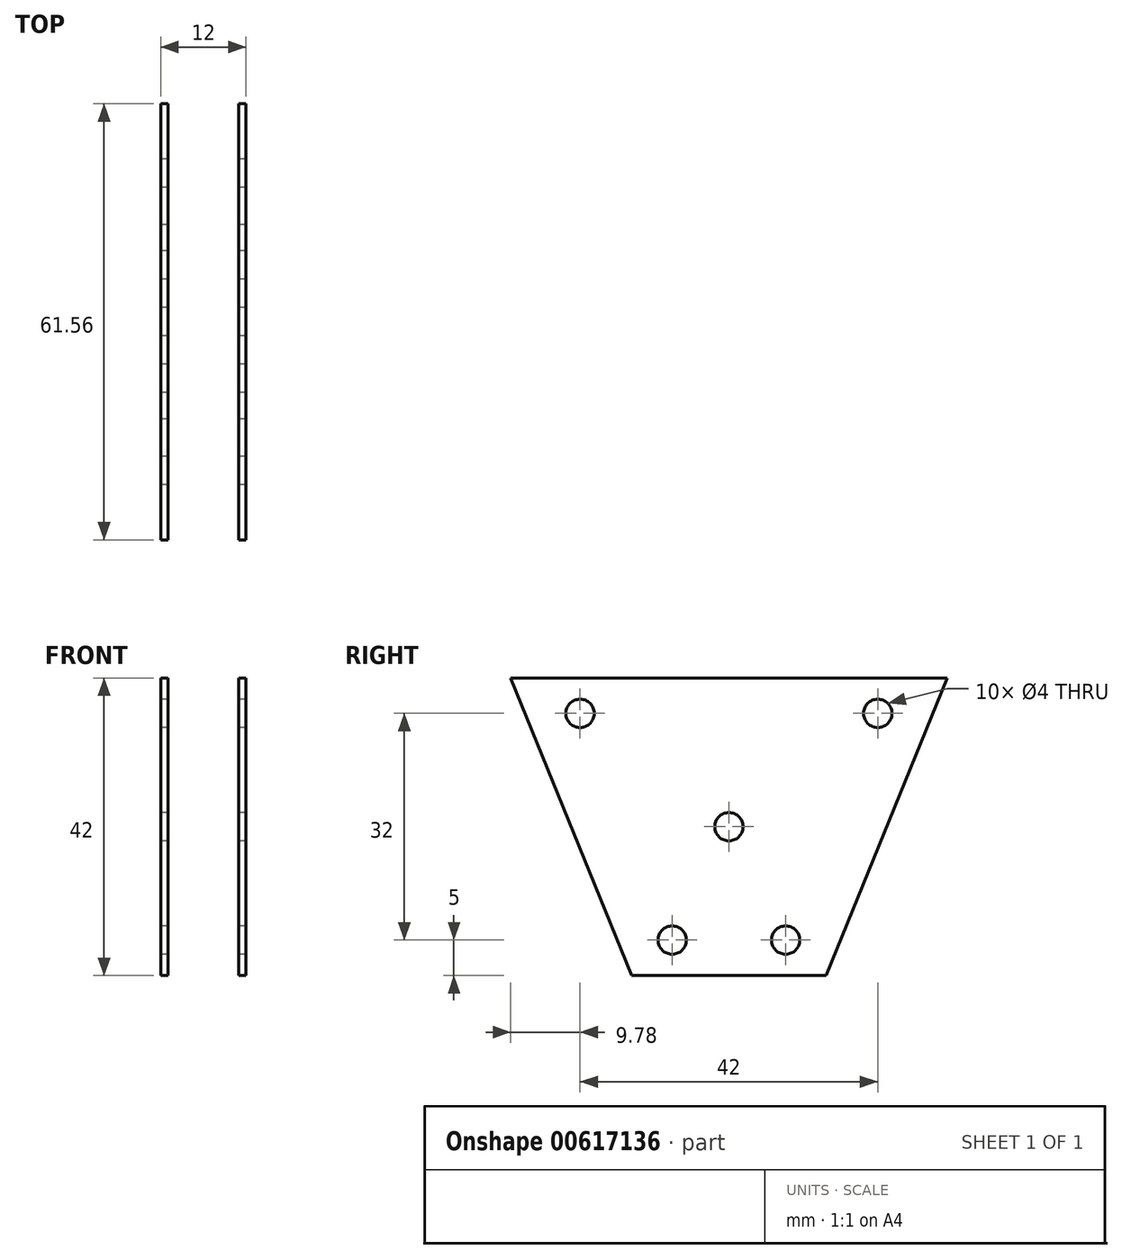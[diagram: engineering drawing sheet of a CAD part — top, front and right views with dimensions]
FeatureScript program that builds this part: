
annotation { "Feature Type Name" : "Feature", "Feature Type Description" : "" }
export const myFeature = defineFeature(function(context is Context, id is Id, definition is map)
    precondition{}
    {
        {
            var Q0;
            Q0=qCreatedBy(makeId("Right.planeOp"),FACE);
            var sketch = newSketch(context, id + "F0", { "sketchPlane" : qUnion([Q0])});
            skLineSegment(sketch, "E0", {"start": v(0, 21) * mm, "end": v(-30.78, 21) * mm});
            skLineSegment(sketch, "E1", {"start": v(-30.78, 21) * mm, "end": v(-13.7, -21) * mm});
            skLineSegment(sketch, "E2", {"start": v(-13.7, -21) * mm, "end": v(0, -21) * mm});
            skCircle(sketch, "E3", {"center": v(-21, 16) * mm, "radius": 2 * mm});
            skCircle(sketch, "E4", {"center": v(-8, -16) * mm, "radius": 2 * mm});
            skLineSegment(sketch, "E5.MirrorCS", {"start": v(30.78, 21) * mm, "end": v(13.7, -21) * mm});
            skLineSegment(sketch, "E6.MirrorCS", {"start": v(0, 21) * mm, "end": v(30.78, 21) * mm});
            skLineSegment(sketch, "E7.MirrorCS", {"start": v(13.7, -21) * mm, "end": v(0, -21) * mm});
            skCircle(sketch, "E8.MirrorC", {"center": v(21, 16) * mm, "radius": 2 * mm});
            skCircle(sketch, "E9.MirrorC", {"center": v(8, -16) * mm, "radius": 2 * mm});
            skCircle(sketch, "E10", {"center": v(0, 0) * mm, "radius": 2 * mm});
            skSolve(sketch);
        }
        {
            var Q0;
            Q0 = qSketchRegion(id + "F0", true);
            extrude(context, id + "F1", {"entities" : qUnion([Q0]), "endBound" : BoundingType.SYMMETRIC, "depth" : 12 * mm, "offsetDistance" : 25 * mm});
        }
        {
            var Q0;
            Q0=qCreatedBy(makeId("Front.planeOp"),FACE);
            var sketch = newSketch(context, id + "F2", { "sketchPlane" : qUnion([Q0])});
            skLineSegment(sketch, "E11.bottom", {"start": v(5, -35.57) * mm, "end": v(-5, -35.57) * mm});
            skLineSegment(sketch, "E11.top", {"start": v(5, 35.57) * mm, "end": v(-5, 35.57) * mm});
            skLineSegment(sketch, "E11.left", {"start": v(5, -35.57) * mm, "end": v(5, 35.57) * mm});
            skLineSegment(sketch, "E11.right", {"start": v(-5, -35.57) * mm, "end": v(-5, 35.57) * mm});
            skPoint(sketch, "E11.middle", {"position": v(0, 0) * mm});
            skSolve(sketch);
        }
        {
            var Q0;
            Q0 = qSketchRegion(id + "F2", true);
            extrude(context, id + "F3", {"entities" : qUnion([Q0]), "operationType" : NewBodyOperationType.REMOVE, "endBound" : BoundingType.SYMMETRIC, "oppositeDirection" : true, "depth" : 100 * mm, "offsetDistance" : 25 * mm});
        }
    });
